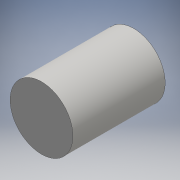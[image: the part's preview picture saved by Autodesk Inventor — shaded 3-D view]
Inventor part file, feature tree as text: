
AUTODESK INVENTOR PART (.ipt)
format: ipt  version: 2016 (Build 200138000, 138)  size: 112,128 bytes
history: native  units: mm
features: hole x4, extrude x2, sketch x2, other x1
ambient origin geometry x8: Origin, YZ Plane, XZ Plane, XY Plane, X Axis, Y Axis, Z Axis, Center Point
bodies: Body1 (feature_tree)
feature tree (9):
  other  "ソリッド1"
  extrude  "押し出し1"  Depth=40.0mm
  extrude  "押し出し2"  Depth=58.7mm TaperAngle=0.0deg
  hole  "穴1"  [1 undecoded]
  hole  "穴2"  [1 undecoded]
  hole  "穴3"  [1 undecoded]
  hole  "穴4"  [1 undecoded]
  sketch  "スケッチ1"
  sketch  "スケッチ2"
note: 4 required parameter values undecoded (feature->parameter linkage not recoverable at this tier; creation-order binding heuristic only, values carry confidence <= 0.55)
